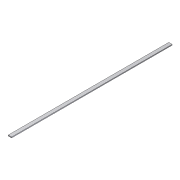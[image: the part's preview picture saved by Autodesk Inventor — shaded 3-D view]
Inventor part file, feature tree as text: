
AUTODESK INVENTOR PART (.ipt)
format: ipt  version: unknown  size: 159,744 bytes
history: native  units: in
note: dims shown in document units (in); Inventor stores cm internally (conversion verified against a paired STEP export)
features: extrude x1, sketch x1
ambient origin geometry x8: Origin, YZ Plane, XZ Plane, XY Plane, X Axis, Y Axis, Z Axis, Center Point
bodies: Solid1 (feature_tree)
feature tree (2):
  extrude  "Extrusion1"  Depth=1.0in
  sketch  "Sketch1"  dims[d0=0.25in d1=1.0in d2=47.5in d3=0.0in]
